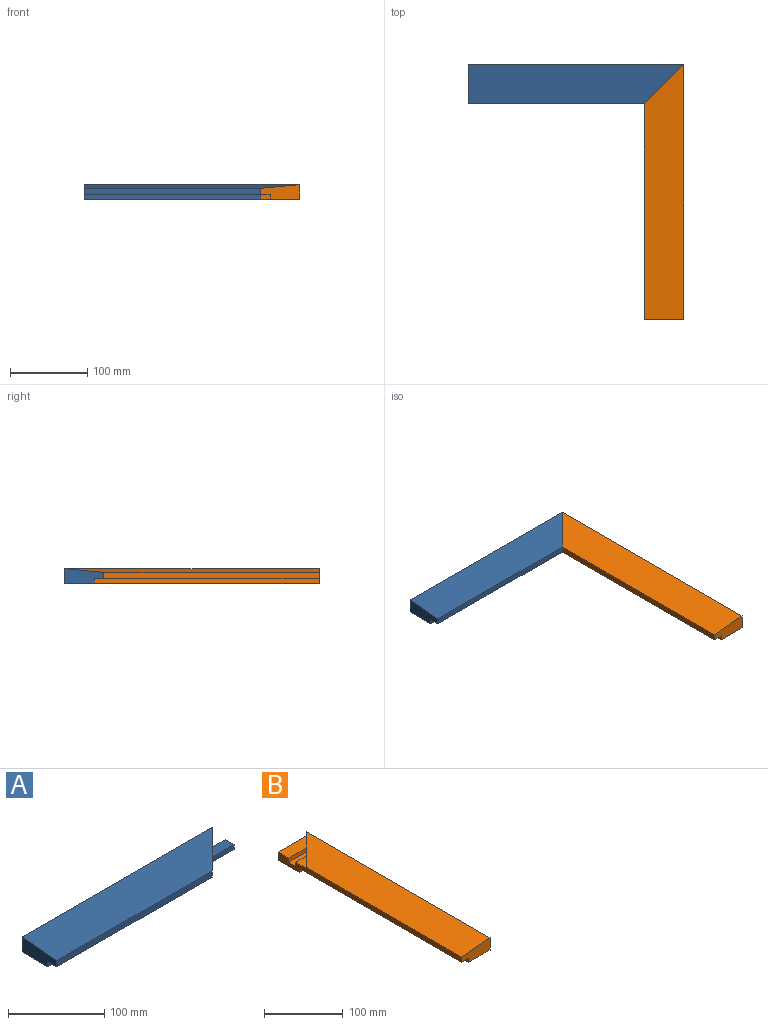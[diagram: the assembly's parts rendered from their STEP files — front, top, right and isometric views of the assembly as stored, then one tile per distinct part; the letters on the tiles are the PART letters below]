
ASSEMBLY  parts=2 mates=1
PART A: 16 faces, bbox 279.4x50.8x19.1 mm
  f0: plane 228.6x7.94mm, normal (0,-1,0), area 1814.5mm2, adj f1,f2,f8,f13,f14
  f1: plane 50.8x19.05mm, normal (-1,0,0), area 766.1mm2, adj f0,f6,f7,f13,f14,f15
  f2: plane 50.8x50.8mm, normal (0.71,-0.71,0), area 285.1mm2, adj f0,f5,f6,f9,f11,f13
  f3: plane 12.7x6.35mm, normal (1,0,0), area 80.6mm2, adj f4,f5,f10,f12
  f4: plane 50.8x12.7mm, normal (0,0,-1), area 645.2mm2, adj f3,f8,f10,f12
  f5: plane 31.75x12.7mm, normal (0,0,1), area 322.6mm2, adj f2,f3,f10,f12
  f6: plane 279.4x19.05mm, normal (0,1,0), area 4677.4mm2, adj f1,f2,f7,f8,f9,f13
  f7: plane 228.6x38.1mm, normal (0,0,-1), area 8709.7mm2, adj f1,f6,f8,f15
  f8: plane 50.8x12.7mm, normal (1,0,0), area 483.9mm2, adj f0,f4,f6,f7,f9,f10,f11,f12
  f9: plane 50.8x19.05mm, normal (0,0,-1), area 786.3mm2, adj f2,f6,f8,f10
  f10: plane 50.8x6.35mm, normal (0,1,0), area 322.6mm2, adj f3,f4,f5,f8,f9
  f11: plane 19.05x19.05mm, normal (0,0,-1), area 181.5mm2, adj f2,f8,f12
  f12: plane 50.8x6.35mm, normal (0,-1,0), area 322.6mm2, adj f3,f4,f5,f8,f11
  f13: plane 279.4x50.8mm, normal (0,-0.09,1), area 12959.8mm2, adj f0,f1,f2,f6
  f14: plane 228.6x12.7mm, normal (0,0,-1), area 2903.2mm2, adj f0,f1,f8,f15
  f15: plane 228.6x6.35mm, normal (0,-1,0), area 1451.6mm2, adj f1,f7,f8,f14
PART B: 16 faces, bbox 50.8x330.2x19.1 mm
  f0: plane 330.2x14.29mm, normal (-1,0,0), area 2701.6mm2, adj f1,f2,f3,f5,f6,f7,f8,f9
  f1: plane 50.8x19.05mm, normal (0,-1,0), area 766.1mm2, adj f0,f3,f4,f12,f14,f15
  f2: plane 19.05x19.05mm, normal (0,0,1), area 181.5mm2, adj f0,f6,f11
  f3: plane 330.2x50.8mm, normal (0,0,-1), area 13064.5mm2, adj f0,f1,f4,f5,f13,f14
  f4: plane 330.2x19.05mm, normal (1,0,0), area 6208.5mm2, adj f1,f3,f5,f6,f8,f9,f10,f11
  f5: plane 50.8x12.7mm, normal (0,1,0), area 645.2mm2, adj f0,f3,f4,f7
  f6: plane 50.8x50.8mm, normal (-0.71,0.71,0), area 283.5mm2, adj f0,f2,f4,f7,f8,f10,f11,f12
  f7: plane 50.8x19.05mm, normal (0,0,1), area 786.3mm2, adj f0,f5,f6,f8
  f8: plane 50.8x6.44mm, normal (0,-1,0), area 324.3mm2, adj f0,f4,f6,f7,f9,f10
  f9: plane 50.8x12.7mm, normal (0,0,1), area 645.2mm2, adj f0,f4,f8,f11
  f10: plane 31.75x12.7mm, normal (0,0,-1), area 322.6mm2, adj f4,f6,f8,f11
  f11: plane 50.8x6.44mm, normal (0,1,0), area 325.4mm2, adj f0,f2,f4,f6,f9,f10
  f12: plane 330.2x50.8mm, normal (-0.09,0,1), area 15551.7mm2, adj f0,f1,f4,f6
  f13: plane 12.7x6.35mm, normal (0,-1,0), area 80.6mm2, adj f0,f3,f14,f15
  f14: plane 292.1x6.35mm, normal (-1,0,0), area 1854.8mm2, adj f1,f3,f13,f15
  f15: plane 292.1x12.7mm, normal (0,0,-1), area 3709.7mm2, adj f0,f1,f13,f14
PLACE A t=(6.52,96.39,-134.71)mm
PLACE B t=(-44.28,96.39,-96.25)mm
MATE planar A.f4 <-> B.f9  axis (0,0,-1) through (-18.88,70.99,-89.9)mm
